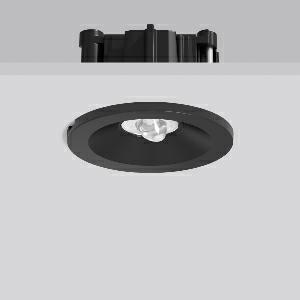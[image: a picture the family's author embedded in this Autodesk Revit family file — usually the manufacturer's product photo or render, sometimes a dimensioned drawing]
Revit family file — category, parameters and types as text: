
# Revit family: turia_l_672562_003_f2c0
name_source: partatom
category: Lighting Fixtures
units: mm (PartAtom-declared; Revit-internal decimal feet)

## family parameters
Cut with Voids When Loaded = No
Host = Face
Light Source = No
Part Type = Normal
Room Calculation Point = No
Round Connector Dimension = Use Diameter
Shared = No

## types (1)
- TURIA L (1 x LED Modul 765, 220 lm, 6500)
    Apparent Load = 4 VA
    CIE Flux Codes = 70 91 99 100 100
    Color Rendering = 70
    Color Temperature = 6500
    Default Elevation = 1800 mm
    Description = Series: TURIA L
Round emergency luminaire for escape route lighting. With asymmetrical beam plastic lenses for illuminating rescue facilities. Suitable for connection to central battery systems. With enclosed separate ceiling mounting ring also suitable for ceiling cut-outs of Ø 68 mm. 
Colour: black
Diameter: 62 mm
Height: 3 mm
Cut-out diameter: 54-68 mm
Recess height: 76-162 mm
Luminaire: recess height: 42 mm
Weight: 230 g
Operating mode: non-maintained power mode
Lamp: LED
Socket: without socket
Colour temperature: 6500K
Colour rendering index (CRI): 70
System power: 3.8 W
Rated luminous flux: 220 lm
Luminous flux, emergency: 220 lm
System power, emergency: 3.8 W
Control gear: Regulated power supply
Protection class: II
Type of protection: IP 20
    Height = 0 mm  [stored 0 ft]
    Lamp = 1 x LED Modul 765
    Lamp Light Flux = 220 lm
    Lamp count = 1
    Length = 62 mm  [stored 0.203412 ft]
    Lifetime = 50000 h
    Luminous efficacy = 58 lm/W
    Manufacturer = RZB
    ModVariant = No
    Model = 672562.003
    Mounting Place = Ceiling
    Mounting Type = Recessed
    Number of Poles = 1
    OnlyDefault = Yes
    Power Factor = 1
    Product Name = TURIA L
    Product group = Recessed ceiling luminaires
    ProductGroupID = 405
    Protection Class = Protection class II
    Protection Degree = IP 20
    RLX_Detail_Level = 1
    RLX_Emergency_Light_Flux = 220 lm
    RLX_Emergency_Type = 3
    RLX_Emergency_Type_DB = Yes
    RlxData = <blob elided: 57993 chars, md5=7be1a787>
    Socket = socket
    Standby Power = 0 W
    System Light Flux = 220 lm
    System Power = 4 W
    Type Comments = Product without accessories
    Type Image = 672561.003.jpg
    URL = http://relux.com
    VarID = ---
    Voltage = 230 V
    Voltage Range = 220-240 V
    Weight = 0.00 kg
    Width = 0 mm  [stored 0 ft]

note: [stored X ft] marks values corroborated as IEEE doubles in the binary element streams (Revit-internal decimal feet)

## geometry (parser evidence)
native form markers: Blend x4, Sweep x13
no freeform markers — native parametric forms only
